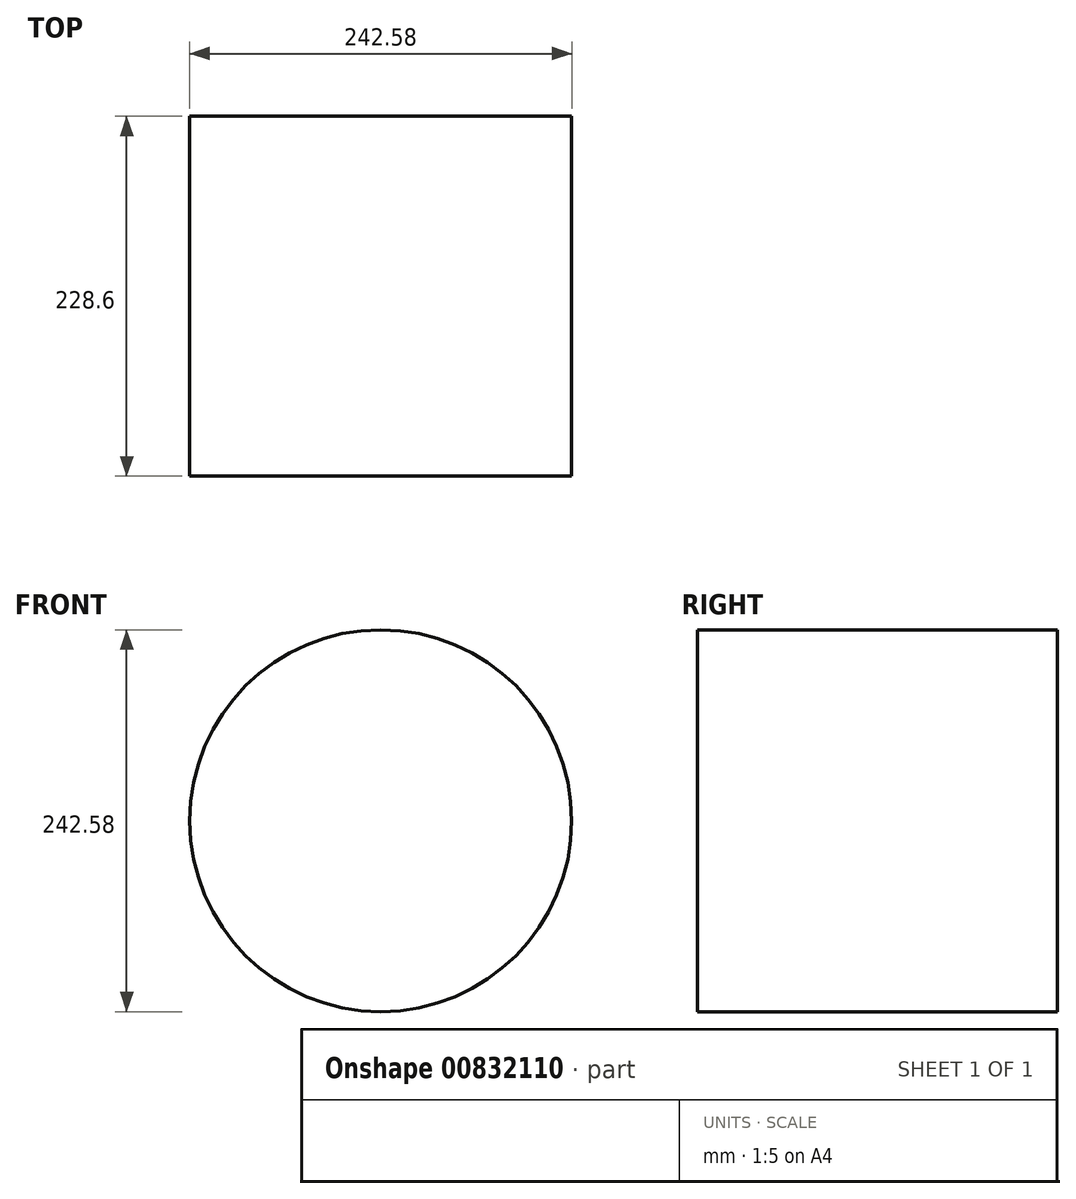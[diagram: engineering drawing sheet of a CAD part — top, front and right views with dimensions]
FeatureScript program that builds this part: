
annotation { "Feature Type Name" : "Feature", "Feature Type Description" : "" }
export const myFeature = defineFeature(function(context is Context, id is Id, definition is map)
    precondition{}
    {
        {
            var Q0;
            Q0=qCreatedBy(makeId("Front.planeOp"),FACE);
            var sketch = newSketch(context, id + "F0", { "sketchPlane" : qUnion([Q0])});
            skCircle(sketch, "E0", {"center": v(0, 0) * mm, "radius": 121.29 * mm});
            skSolve(sketch);
        }
        {
            var Q0;
            Q0 = qSketchRegion(id + "F0", true);
            extrude(context, id + "F1", {"entities" : qUnion([Q0]), "depth" : 228.6 * mm, "offsetDistance" : 25.4 * mm});
        }
    });
